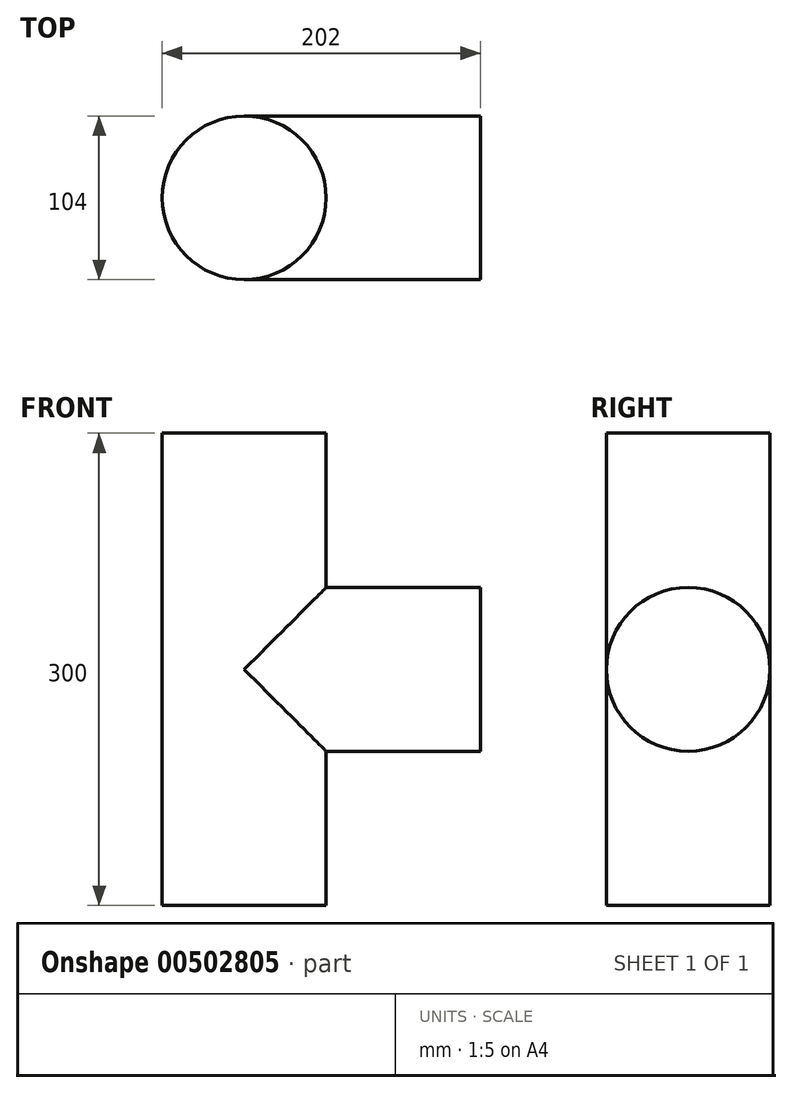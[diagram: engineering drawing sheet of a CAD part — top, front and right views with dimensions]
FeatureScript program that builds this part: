
annotation { "Feature Type Name" : "Feature", "Feature Type Description" : "" }
export const myFeature = defineFeature(function(context is Context, id is Id, definition is map)
    precondition{}
    {
        {
            var Q0;
            Q0=qCreatedBy(makeId("Top.planeOp"),FACE);
            var sketch = newSketch(context, id + "F0", { "sketchPlane" : qUnion([Q0])});
            skCircle(sketch, "E0", {"center": v(0, 0) * mm, "radius": 52 * mm});
            skSolve(sketch);
        }
        {
            var Q0;
            Q0 = qSketchRegion(id + "F0", true);
            extrude(context, id + "F1", {"entities" : qUnion([Q0]), "depth" : 300 * mm, "symmetric" : true});
        }
        {
            var Q0;
            Q0=qCreatedBy(makeId("Right.planeOp"),FACE);
            var sketch = newSketch(context, id + "F2", { "sketchPlane" : qUnion([Q0])});
            skCircle(sketch, "E1", {"center": v(0, 0) * mm, "radius": 52 * mm});
            skSolve(sketch);
        }
        {
            var Q0;
            Q0 = qSketchRegion(id + "F2", true);
            extrude(context, id + "F3", {"entities" : qUnion([Q0]), "operationType" : NewBodyOperationType.ADD, "depth" : 150 * mm});
        }
    });
